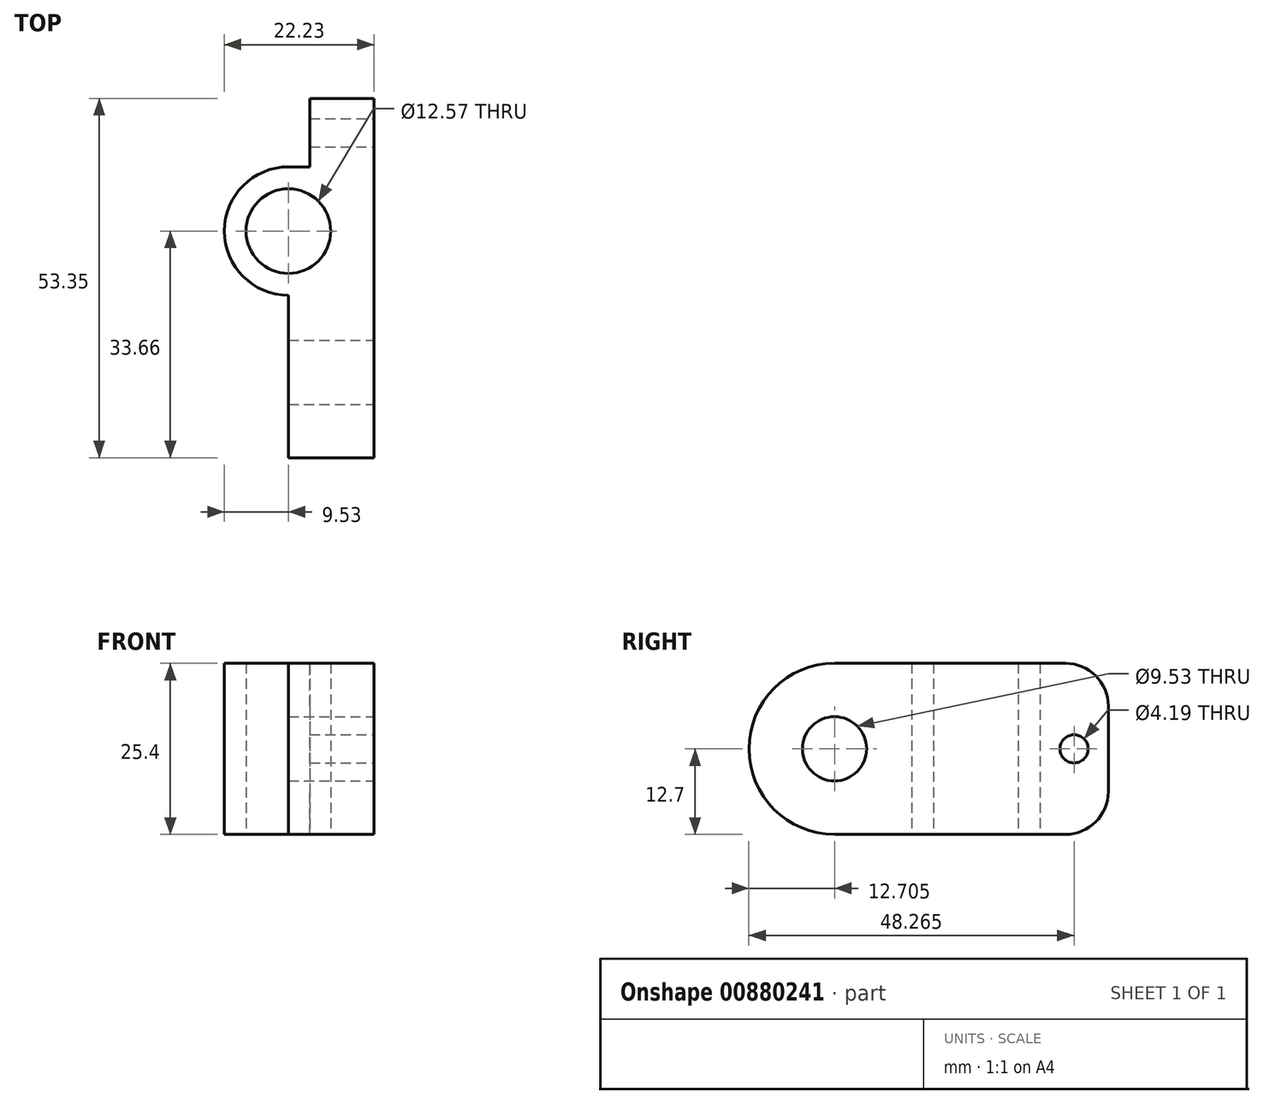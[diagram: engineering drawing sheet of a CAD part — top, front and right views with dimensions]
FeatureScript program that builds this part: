
annotation { "Feature Type Name" : "Feature", "Feature Type Description" : "" }
export const myFeature = defineFeature(function(context is Context, id is Id, definition is map)
    precondition{}
    {
        {
            var Q0;
            Q0=qCreatedBy(makeId("Top.planeOp"),FACE);
            var sketch = newSketch(context, id + "F0", { "sketchPlane" : qUnion([Q0])});
            skCircle(sketch, "E0", {"center": v(0, 0) * mm, "radius": 6.29 * mm});
            skLineSegment(sketch, "E1.bottom", {"start": v(9.53, 9.53) * mm, "end": v(0, 9.53) * mm});
            skLineSegment(sketch, "E1.top", {"start": v(9.53, -9.53) * mm, "end": v(0, -9.53) * mm});
            skLineSegment(sketch, "E1.left", {"start": v(9.53, 9.53) * mm, "end": v(9.53, -9.53) * mm});
            skLineSegment(sketch, "E1.right", {"start": v(-9.53, 0) * mm, "end": v(-9.53, 0) * mm});
            skPoint(sketch, "E2.visualSharp", {"position": v(-9.53, -9.53) * mm});
            skArc(sketch, "E2.filletArc", {"start": v(-9.53, 0) * mm, "mid": v(-6.74, -6.74) * mm, "end": v(0, -9.53) * mm});
            skPoint(sketch, "E3.visualSharp", {"position": v(9.53, 9.53) * mm});
            skPoint(sketch, "E4.visualSharp", {"position": v(9.53, -9.53) * mm});
            skPoint(sketch, "E5.visualSharp", {"position": v(-9.53, 9.53) * mm});
            skArc(sketch, "E5.filletArc", {"start": v(0, 9.53) * mm, "mid": v(-6.74, 6.74) * mm, "end": v(-9.53, 0) * mm});
            skSolve(sketch);
        }
        {
            var Q0;
            Q0=makeQuery(id+"F0.imprint","IMPRINT",FACE,{"disambiguationData":[TD([[makeQuery(id+"F0.imprint","IMPRINT",EDGE,{"derivedFrom":sQuery(id+"F0.wireOp",EDGE,"E0")}),-1.0]])]});
            extrude(context, id + "F1", {"entities" : qUnion([Q0]), "depth" : 25.4 * mm});
        }
        {
            var Q0;
            Q0=makeQuery(id+"F1.opExtrude","SWEPT_FACE",FACE,{"disambiguationData":[OSD([sQuery(id+"F0.wireOp",EDGE,"E1.left")])]});
            var sketch = newSketch(context, id + "F2", { "sketchPlane" : qUnion([Q0])});
            skCircle(sketch, "E6", {"center": v(-20.96, 12.7) * mm, "radius": 4.76 * mm});
            skArc(sketch, "E7", {"start": v(-20.96, 25.4) * mm, "mid": v(-33.66, 12.7) * mm, "end": v(-20.95, 0) * mm});
            skLineSegment(sketch, "E8", {"start": v(-9.53, 12.7) * mm, "end": v(-20.96, 12.7) * mm, "construction": true});
            skLineSegment(sketch, "E9", {"start": v(-9.53, 25.4) * mm, "end": v(-20.96, 25.4) * mm});
            skLineSegment(sketch, "E10", {"start": v(-9.52, 0) * mm, "end": v(-20.96, 0) * mm});
            skLineSegment(sketch, "E11.0", {"start": v(-9.53, 25.4) * mm, "end": v(-9.53, 0) * mm});
            skSolve(sketch);
        }
        {
            var Q0;
            Q0=qSketchRegion(id+"F2",true);
            extrude(context, id + "F3", {"entities" : qUnion([Q0]), "operationType" : NewBodyOperationType.ADD, "oppositeDirection" : true, "depth" : 9.52 * mm});
        }
        {
            var Q0;
            Q0=makeQuery(id+"F3.boolean.opBoolean","MERGE",FACE,{"derivedFrom":[makeQuery(id+"F1.opExtrude","SWEPT_FACE",FACE,{"disambiguationData":[OSD([sQuery(id+"F0.wireOp",EDGE,"E1.left")])]}),makeQuery(id+"F3.opExtrude","CAP_FACE",FACE,{"disambiguationData":[OSD([sQuery(id+"F2.wireOp",EDGE,"E6"),sQuery(id+"F2.wireOp",EDGE,"E7"),sQuery(id+"F2.wireOp",EDGE,"E9"),sQuery(id+"F2.wireOp",EDGE,"E10"),sQuery(id+"F2.wireOp",EDGE,"E11.0")])],"isStart":true})]});
            var sketch = newSketch(context, id + "F4", { "sketchPlane" : qUnion([Q0])});
            skCircle(sketch, "E12", {"center": v(14.6, 12.7) * mm, "radius": 2.1 * mm});
            skLineSegment(sketch, "E13", {"start": v(-20.96, 12.7) * mm, "end": v(14.6, 12.7) * mm, "construction": true});
            skLineSegment(sketch, "E14.0", {"start": v(9.53, 25.4) * mm, "end": v(9.53, 0) * mm});
            skLineSegment(sketch, "E15", {"start": v(9.53, 25.4) * mm, "end": v(13.33, 25.4) * mm});
            skLineSegment(sketch, "E16", {"start": v(13.33, 0) * mm, "end": v(9.53, 0) * mm});
            skLineSegment(sketch, "E17", {"start": v(19.68, 19.05) * mm, "end": v(19.68, 6.35) * mm});
            skPoint(sketch, "E18.visualSharp", {"position": v(19.68, 25.4) * mm});
            skArc(sketch, "E18.filletArc", {"start": v(19.69, 19.05) * mm, "mid": v(17.83, 23.54) * mm, "end": v(13.33, 25.4) * mm});
            skPoint(sketch, "E19.visualSharp", {"position": v(19.69, 0) * mm});
            skArc(sketch, "E19.filletArc", {"start": v(13.33, 0) * mm, "mid": v(17.83, 1.86) * mm, "end": v(19.68, 6.35) * mm});
            skSolve(sketch);
        }
        {
            var Q0;
            Q0=qSketchRegion(id+"F4",true);
            extrude(context, id + "F5", {"entities" : qUnion([Q0]), "operationType" : NewBodyOperationType.ADD, "oppositeDirection" : true, "depth" : 6.35 * mm});
        }
        {
            var Q0;
            Q0=makeQuery(id+"F5.boolean.opBoolean","MERGE",FACE,{"derivedFrom":[makeQuery(id+"F3.boolean.opBoolean","MERGE",FACE,{"derivedFrom":[makeQuery(id+"F1.opExtrude","SWEPT_FACE",FACE,{"disambiguationData":[OSD([sQuery(id+"F0.wireOp",EDGE,"E1.left")])]}),makeQuery(id+"F3.opExtrude","CAP_FACE",FACE,{"disambiguationData":[OSD([sQuery(id+"F2.wireOp",EDGE,"E6"),sQuery(id+"F2.wireOp",EDGE,"E7"),sQuery(id+"F2.wireOp",EDGE,"E9"),sQuery(id+"F2.wireOp",EDGE,"E10"),sQuery(id+"F2.wireOp",EDGE,"E11.0")])],"isStart":true})]}),makeQuery(id+"F5.opExtrude","CAP_FACE",FACE,{"disambiguationData":[OSD([sQuery(id+"F4.wireOp",EDGE,"E12"),sQuery(id+"F4.wireOp",EDGE,"E14.0"),sQuery(id+"F4.wireOp",EDGE,"E15"),sQuery(id+"F4.wireOp",EDGE,"E16"),sQuery(id+"F4.wireOp",EDGE,"E17"),sQuery(id+"F4.wireOp",EDGE,"E18.filletArc"),sQuery(id+"F4.wireOp",EDGE,"E19.filletArc")])],"isStart":true})]});
            extrude(context, id + "F6", {"entities" : qUnion([Q0]), "operationType" : NewBodyOperationType.ADD, "depth" : 3.17 * mm});
        }
    });
